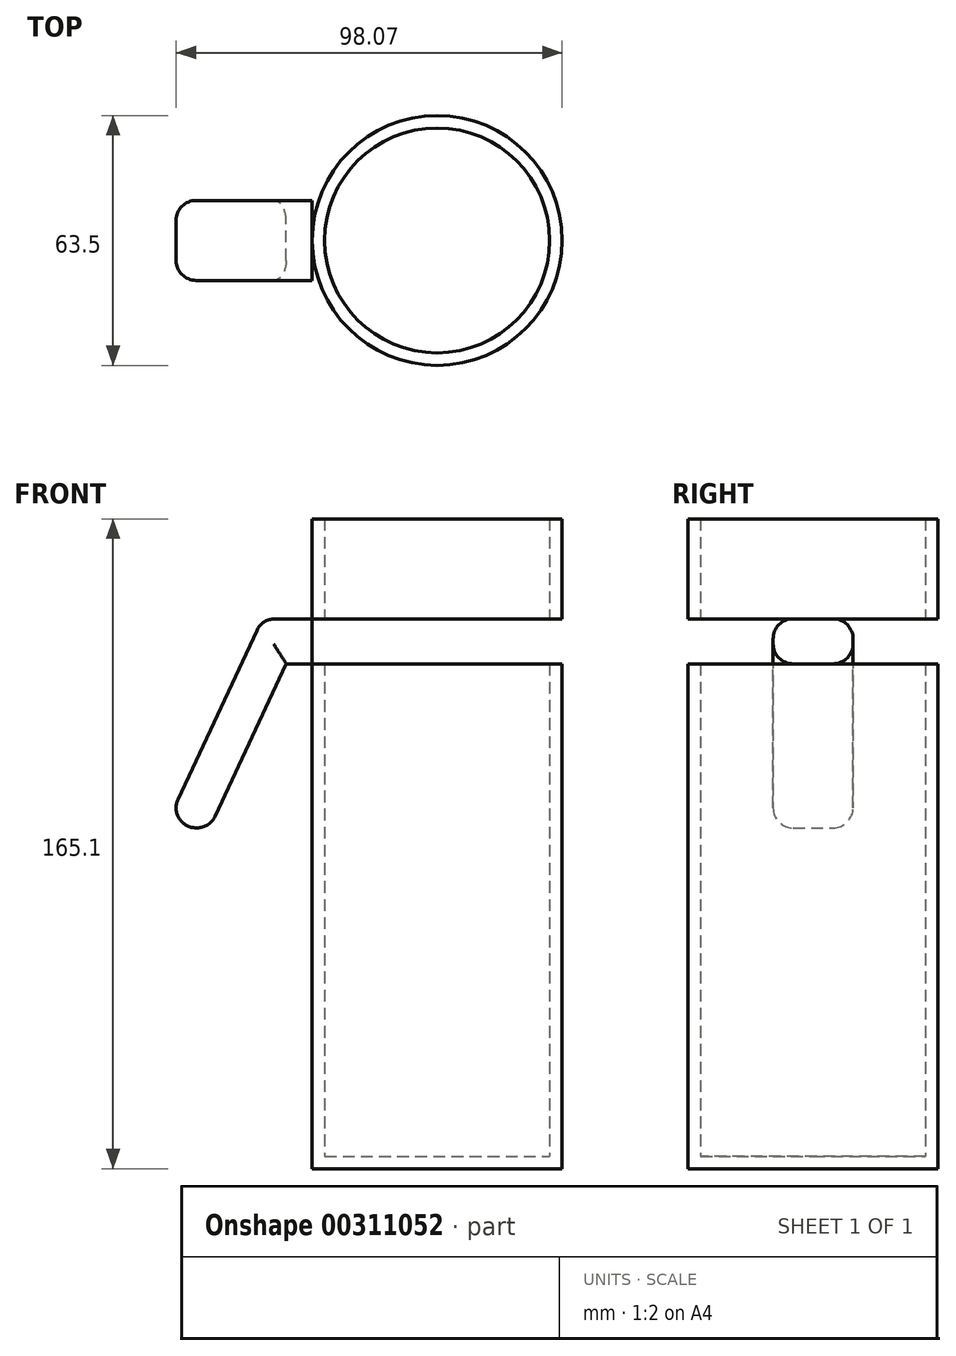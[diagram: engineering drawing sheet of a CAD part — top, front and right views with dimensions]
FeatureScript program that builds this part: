
annotation { "Feature Type Name" : "Feature", "Feature Type Description" : "" }
export const myFeature = defineFeature(function(context is Context, id is Id, definition is map)
    precondition{}
    {
        {
            var Q0;
            Q0=qCreatedBy(makeId("Front.planeOp"),FACE);
            var sketch = newSketch(context, id + "F0", { "sketchPlane" : qUnion([Q0])});
            skLineSegment(sketch, "E0", {"start": v(0, 0) * mm, "end": v(-31.75, 0) * mm});
            skLineSegment(sketch, "E1", {"start": v(-31.75, 0) * mm, "end": v(-31.75, 165.1) * mm});
            skLineSegment(sketch, "E2", {"start": v(0, 0) * mm, "end": v(0, 3.18) * mm});
            skLineSegment(sketch, "E3", {"start": v(0, 3.18) * mm, "end": v(-28.57, 3.17) * mm});
            skLineSegment(sketch, "E4", {"start": v(-28.57, 3.17) * mm, "end": v(-28.57, 165.1) * mm});
            skLineSegment(sketch, "E5", {"start": v(-28.57, 165.1) * mm, "end": v(-31.75, 165.1) * mm});
            skLineSegment(sketch, "E6", {"start": v(-31.75, 165.1) * mm, "end": v(-31.75, 139.7) * mm, "construction": true});
            skLineSegment(sketch, "E7", {"start": v(-28.58, 139.7) * mm, "end": v(-44.45, 139.7) * mm});
            skLineSegment(sketch, "E8", {"start": v(-44.45, 139.7) * mm, "end": v(-69.22, 86.6) * mm});
            skLineSegment(sketch, "E9", {"start": v(-69.22, 86.6) * mm, "end": v(-57.78, 86.6) * mm});
            skLineSegment(sketch, "E10", {"start": v(-57.78, 86.6) * mm, "end": v(-38.35, 128.27) * mm});
            skLineSegment(sketch, "E11", {"start": v(-38.35, 128.27) * mm, "end": v(-28.58, 128.27) * mm});
            skLineSegment(sketch, "E12", {"start": v(-28.58, 128.27) * mm, "end": v(-28.58, 139.7) * mm});
            skLineSegment(sketch, "E13", {"start": v(-28.57, 165.1) * mm, "end": v(-28.57, 139.7) * mm, "construction": true});
            skSolve(sketch);
        }
        {
            var Q0;
            {var subQ3=sQuery(id+"F0.wireOp",EDGE,"E0");Q0=makeQuery(id+"F0.imprint","IMPRINT",FACE,{"disambiguationData":[TD([[makeQuery(id+"F0.imprint","IMPRINT",EDGE,{"derivedFrom":subQ3}),-1.0]])]});}
            var Q1;
            {var subQ0=sQuery(id+"F0.wireOp",EDGE,"E5");Q1=makeQuery(id+"F0.imprint","IMPRINT",FACE,{"disambiguationData":[TD([[makeQuery(id+"F0.imprint","IMPRINT",EDGE,{"derivedFrom":subQ0}),1.0]])]});}
            var Q2;
            {var subQ5=sQuery(id+"F0.wireOp",EDGE,"E12");Q2=makeQuery(id+"F0.imprint","IMPRINT",FACE,{"disambiguationData":[TD([[makeQuery(id+"F0.imprint","IMPRINT",EDGE,{"derivedFrom":subQ5}),1.0]])]});}
            var Q3;
            Q3=sQuery(id+"F0.wireOp",EDGE,"E2");
            revolve(context, id + "F1", {"entities" : qUnion([Q0, Q1, Q2]), "axis" : qUnion([Q3]), "revolveType" : RevolveType.FULL});
        }
        {
            var Q0;
            {var subQ0=sQuery(id+"F0.wireOp",EDGE,"E8");Q0=makeQuery(id+"F0.imprint","IMPRINT",FACE,{"disambiguationData":[TD([[makeQuery(id+"F0.imprint","IMPRINT",EDGE,{"derivedFrom":subQ0}),1.0]])]});}
            var Q1;
            {var subQ5=sQuery(id+"F0.wireOp",EDGE,"E12");Q1=makeQuery(id+"F0.imprint","IMPRINT",FACE,{"disambiguationData":[TD([[makeQuery(id+"F0.imprint","IMPRINT",EDGE,{"derivedFrom":subQ5}),1.0]])]});}
            extrude(context, id + "F2", {"entities" : qUnion([Q0, Q1]), "operationType" : NewBodyOperationType.ADD, "endBound" : BoundingType.SYMMETRIC, "depth" : 20.32 * mm});
        }
        {
            var Q0;
            Q0=makeQuery(id+"F2.opExtrude","CAP_EDGE",EDGE,{"disambiguationData":[OSD([sQuery(id+"F0.wireOp",EDGE,"E8")])],"isStart":true});
            var Q1;
            Q1=makeQuery(id+"F2.opExtrude","CAP_EDGE",EDGE,{"disambiguationData":[OSD([sQuery(id+"F0.wireOp",EDGE,"E8")])],"isStart":false});
            var Q2;
            Q2=makeQuery(id+"F2.opExtrude","CAP_EDGE",EDGE,{"disambiguationData":[OSD([sQuery(id+"F0.wireOp",EDGE,"E7")])],"isStart":false});
            var Q3;
            Q3=makeQuery(id+"F2.opExtrude","CAP_EDGE",EDGE,{"disambiguationData":[OSD([sQuery(id+"F0.wireOp",EDGE,"E7")])],"isStart":true});
            var Q4;
            Q4=makeQuery(id+"F2.opExtrude","SWEPT_EDGE",EDGE,{"disambiguationData":[OSD([sQuery(id+"F0.wireOp",EDGE,"E7"),sQuery(id+"F0.wireOp",EDGE,"E8")])]});
            var Q5;
            Q5=makeQuery(id+"F2.opExtrude","CAP_EDGE",EDGE,{"disambiguationData":[OSD([sQuery(id+"F0.wireOp",EDGE,"E10")])],"isStart":false});
            var Q6;
            Q6=makeQuery(id+"F2.opExtrude","CAP_EDGE",EDGE,{"disambiguationData":[OSD([sQuery(id+"F0.wireOp",EDGE,"E10")])],"isStart":true});
            var Q7;
            Q7=makeQuery(id+"F2.opExtrude","CAP_EDGE",EDGE,{"disambiguationData":[OSD([sQuery(id+"F0.wireOp",EDGE,"E9")])],"isStart":false});
            var Q8;
            Q8=makeQuery(id+"F2.opExtrude","CAP_EDGE",EDGE,{"disambiguationData":[OSD([sQuery(id+"F0.wireOp",EDGE,"E9")])],"isStart":true});
            var Q9;
            Q9=makeQuery(id+"F2.opExtrude","SWEPT_EDGE",EDGE,{"disambiguationData":[OSD([sQuery(id+"F0.wireOp",EDGE,"E9"),sQuery(id+"F0.wireOp",EDGE,"E10")])]});
            var Q10;
            Q10=makeQuery(id+"F2.opExtrude","SWEPT_EDGE",EDGE,{"disambiguationData":[OSD([sQuery(id+"F0.wireOp",EDGE,"E8"),sQuery(id+"F0.wireOp",EDGE,"E9")])]});
            var Q11;
            Q11=makeQuery(id+"F2.opExtrude","CAP_EDGE",EDGE,{"disambiguationData":[OSD([sQuery(id+"F0.wireOp",EDGE,"E11")])],"isStart":true});
            var Q12;
            Q12=makeQuery(id+"F2.opExtrude","CAP_EDGE",EDGE,{"disambiguationData":[OSD([sQuery(id+"F0.wireOp",EDGE,"E11")])],"isStart":false});
            fillet(context, id + "F3", {"entities" : qUnion([Q0, Q1, Q2, Q3, Q4, Q5, Q6, Q7, Q8, Q9, Q10, Q11, Q12]), "radius" : 5.08 * mm, "tangentPropagation" : true, "allowEdgeOverflow" : false});
        }
    });
